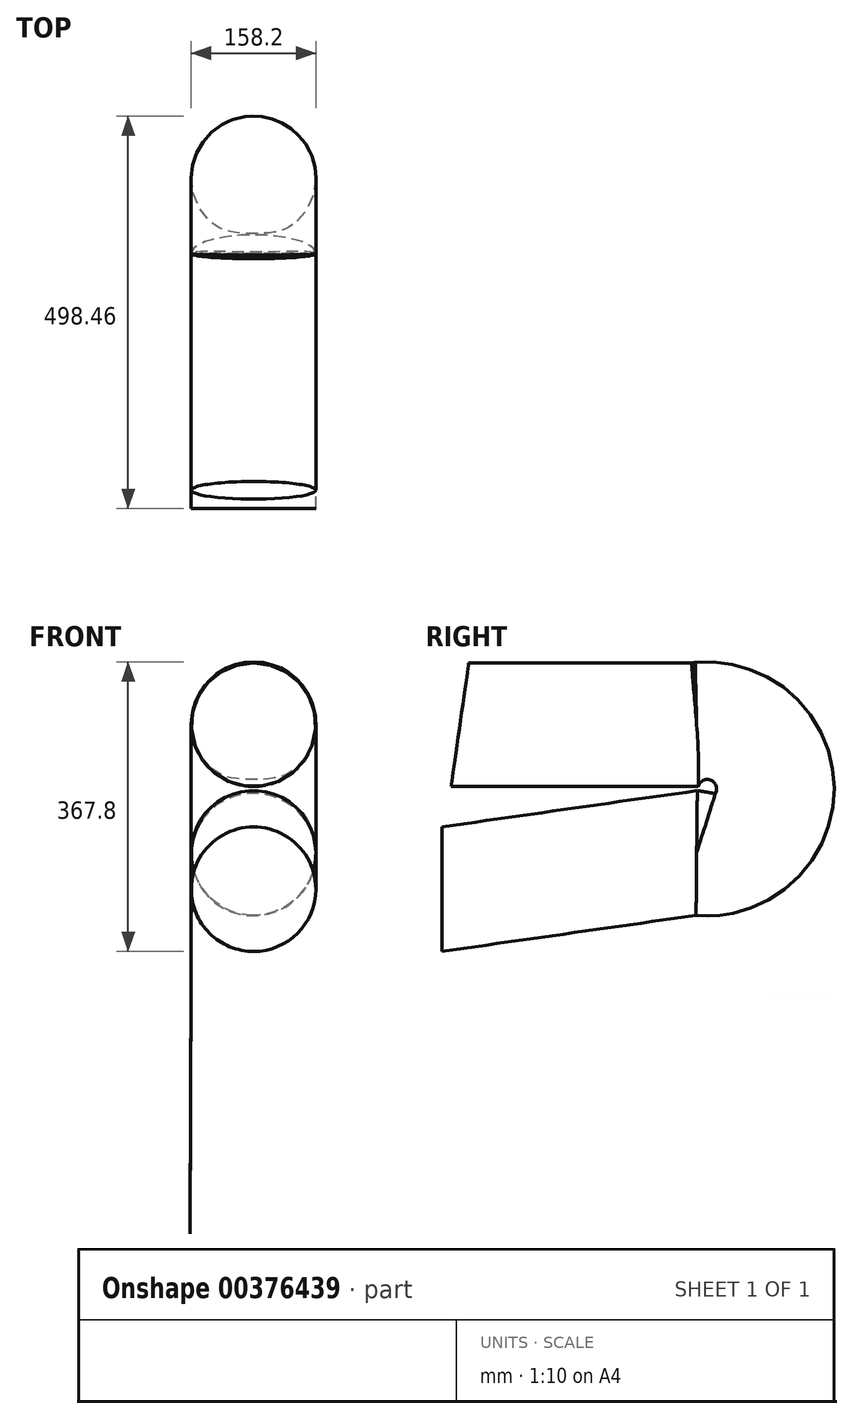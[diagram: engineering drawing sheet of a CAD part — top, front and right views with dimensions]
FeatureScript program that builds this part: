
annotation { "Feature Type Name" : "Feature", "Feature Type Description" : "" }
export const myFeature = defineFeature(function(context is Context, id is Id, definition is map)
    precondition{}
    {
        {
            var Q0;
            Q0=qCreatedBy(makeId("Front.planeOp"),FACE);
            var sketch = newSketch(context, id + "F0", { "sketchPlane" : qUnion([Q0])});
            skCircle(sketch, "E0", {"center": v(0, 0) * mm, "radius": 79.1 * mm});
            skSolve(sketch);
        }
        {
            var Q0;
            Q0=qCreatedBy(makeId("Right.planeOp"),FACE);
            var sketch = newSketch(context, id + "F1", { "sketchPlane" : qUnion([Q0])});
            skLineSegment(sketch, "E1", {"start": v(0, 0) * mm, "end": v(323.72, 46.03) * mm});
            skArc(sketch, "E2", {"start": v(323.72, 46.03) * mm, "mid": v(419.76, 127.46) * mm, "end": v(323.72, 208.9) * mm});
            skLineSegment(sketch, "E3", {"start": v(323.72, 208.9) * mm, "end": v(23.1, 208.9) * mm});
            skSolve(sketch);
        }
        {
            var Q0;
            Q0 = qSketchRegion(id + "F0", true);
            var Q1;
            Q1 = qBodyType(qCreatedBy(id + "F1" ,EDGE), BodyType.WIRE);
            sweep(context, id + "F2", {"profiles" : qUnion([Q0]), "path" : qUnion([Q1])});
        }
        {
            var Q0;
            Q0=qCreatedBy(makeId("Right.planeOp"),FACE);
            var sketch = newSketch(context, id + "F3", { "sketchPlane" : qUnion([Q0])});
            skFitSpline(sketch, "E4.0", {"points": [v(0, -31.13) * mm, v(0, 85.1) * mm, v(0, 253.75) * mm, v(0, 396.18) * mm]});
            skFitSpline(sketch, "E5", {"points": [v(0, 269.86) * mm, v(724.73, 304) * mm], "startDerivative": vector(696.5, 238.6) * mm, "endDerivative": vector(389.63, -636.78) * mm});
            skSolve(sketch);
        }
    });
